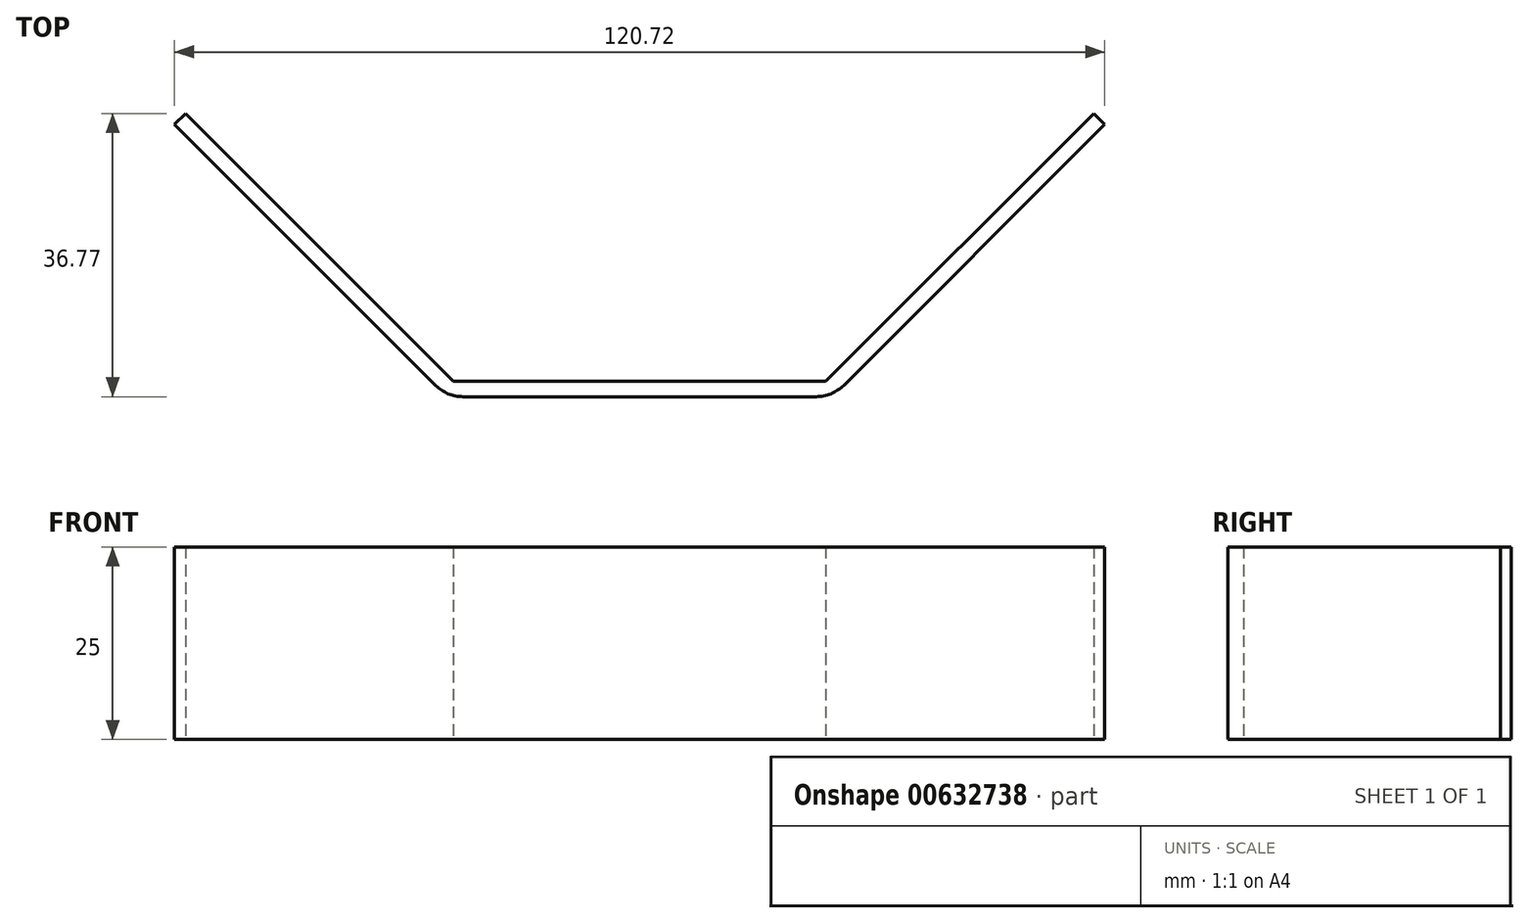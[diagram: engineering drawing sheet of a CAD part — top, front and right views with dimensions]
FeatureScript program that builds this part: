
annotation { "Feature Type Name" : "Feature", "Feature Type Description" : "" }
export const myFeature = defineFeature(function(context is Context, id is Id, definition is map)
    precondition{}
    {
        {
            var Q0;
            Q0=qCreatedBy(makeId("Top.planeOp"),FACE);
            var sketch = newSketch(context, id + "F0", { "sketchPlane" : qUnion([Q0])});
            skLineSegment(sketch, "E0", {"start": v(-60.36, 0) * mm, "end": v(-26.46, -33.9) * mm});
            skLineSegment(sketch, "E1", {"start": v(26.46, -33.9) * mm, "end": v(60.36, 0) * mm});
            skLineSegment(sketch, "E2", {"start": v(-22.93, -35.35) * mm, "end": v(22.93, -35.35) * mm});
            skPoint(sketch, "E3.visualSharp", {"position": v(-25, -35.35) * mm});
            skArc(sketch, "E3.filletArc", {"start": v(-26.46, -33.9) * mm, "mid": v(-24.84, -34.97) * mm, "end": v(-22.93, -35.35) * mm});
            skPoint(sketch, "E4.visualSharp", {"position": v(25, -35.36) * mm});
            skArc(sketch, "E4.filletArc", {"start": v(22.93, -35.35) * mm, "mid": v(24.84, -34.97) * mm, "end": v(26.46, -33.9) * mm});
            skLineSegment(sketch, "E5.0", {"start": v(24.17, -33.35) * mm, "end": v(58.94, 1.41) * mm});
            skLineSegment(sketch, "E5.1", {"start": v(-24.17, -33.36) * mm, "end": v(24.17, -33.35) * mm});
            skLineSegment(sketch, "E5.2", {"start": v(-58.94, 1.41) * mm, "end": v(-24.17, -33.36) * mm});
            skLineSegment(sketch, "E6", {"start": v(-60.36, 0) * mm, "end": v(-58.94, 1.41) * mm});
            skLineSegment(sketch, "E7", {"start": v(60.36, 0) * mm, "end": v(58.94, 1.41) * mm});
            skSolve(sketch);
        }
        {
            var Q0;
            Q0 = qSketchRegion(id + "F0", true);
            extrude(context, id + "F1", {"entities" : qUnion([Q0]), "depth" : 25 * mm, "offsetDistance" : 25 * mm});
        }
    });
